# Revit family: PlumbingFixture_Drain_Galvin_DV100S
name_source: partatom
category: Plumbing Fixtures
revit_build: Autodesk Revit MEP 2012 (Build: 20110916_2132(x64)
units: mm (PartAtom-declared; Revit-internal decimal feet)

## types (2) — shared parameters
Application = PVC/HDPE
Assembly Code = D2040200
BodyMaterial = Metal_Drains_Cast-Iron_15400
CHWFlow_ANZRS = 1.4 L/s
Circulation_ANZRS = Yes
Description = Square Vertical Drain Combination - Standard
DimAdjustableTop = 48 mm  [stored 0.15748 ft]
DimBodyHeight = 81 mm  [stored 0.265748 ft]
DimGrateHeight = 27 mm  [stored 0.0885827 ft]
DimTop = 100 mm  [stored 0.328084 ft]
FilterObject_ANZRS = DV-SX
GrateMaterial = Metal_Drains_Stainless-Steel_15400
Instructions = http://www.galvinengineering.com.au
Keynote = 10800
Manufacturer = Galvin Engineering
ModifiedIssue_ANZRS = 20140526 $
StyleOrType_ANZRS = Drain
Type Comments = Square
URL = www.galvinengineering.com.au
zero-valued in all types: Default Elevation

## per-type parameters (varying)
| type | DimOutlet | OutletRadius_DoNotEdit |
| DV2S04SX - ST/ST 316 | 50 mm  [stored 0.164042 ft] | 25 mm  [stored 0.082021 ft] |
| DV3S04SX - ST/ST 316 | 80 mm  [stored 0.262467 ft] | 40 mm  [stored 0.131234 ft] |

note: column(s) folded — value = type name in every type: Model

note: [stored X ft] marks values corroborated as IEEE doubles in the binary element streams (Revit-internal decimal feet)

## geometry (parser evidence)
native form markers: Blend x2, Sweep x1
no freeform markers — native parametric forms only
